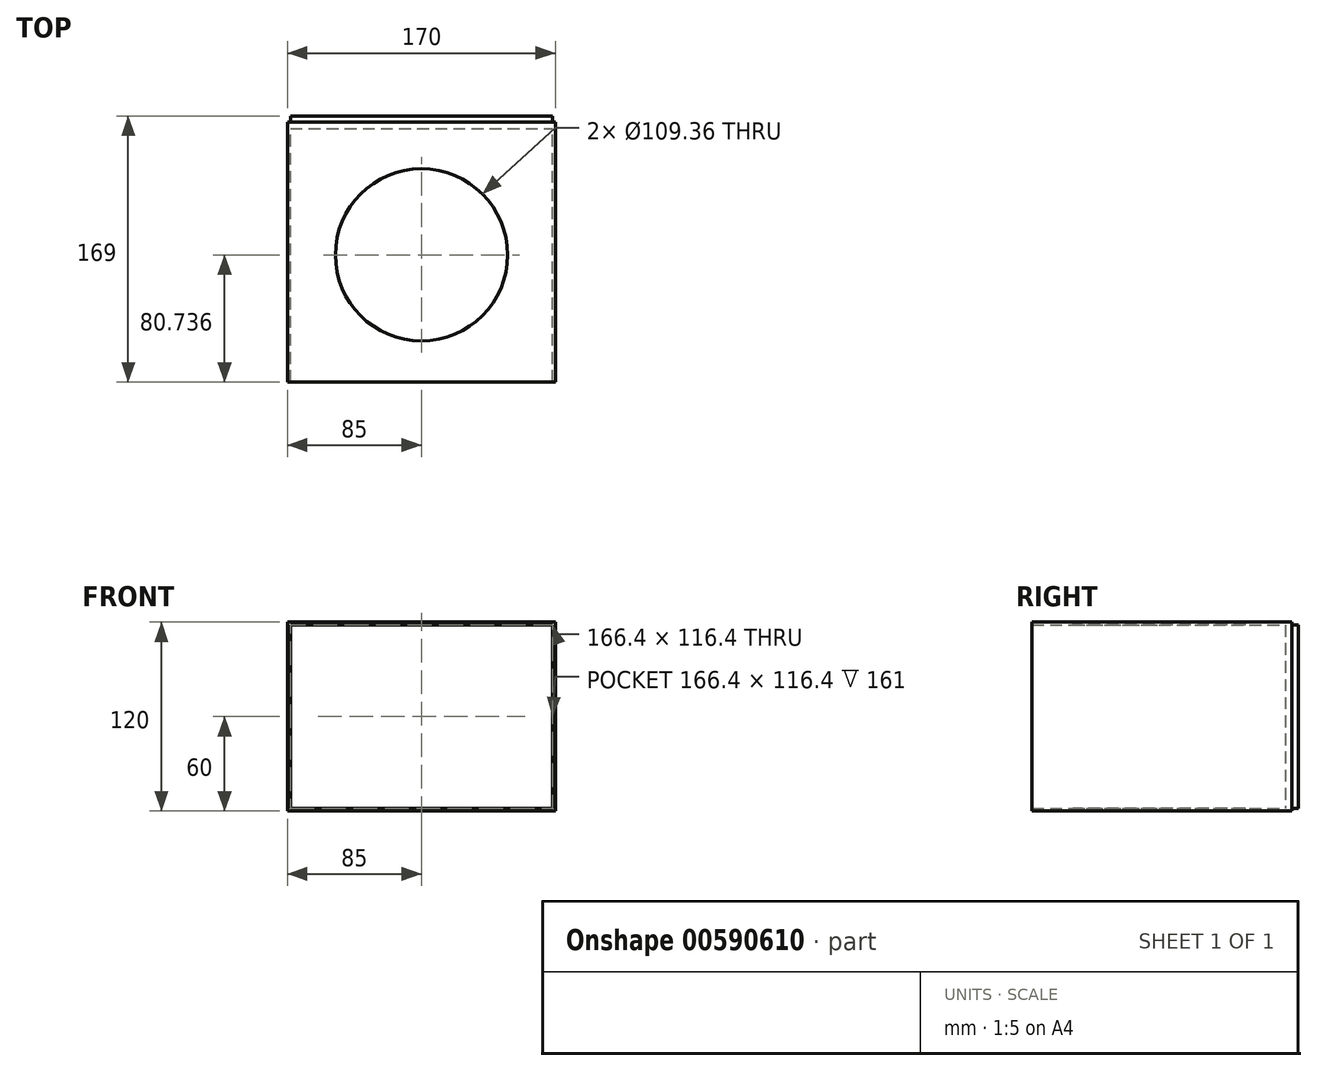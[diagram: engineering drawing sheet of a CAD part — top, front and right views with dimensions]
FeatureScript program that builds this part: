
annotation { "Feature Type Name" : "Feature", "Feature Type Description" : "" }
export const myFeature = defineFeature(function(context is Context, id is Id, definition is map)
    precondition{}
    {
        {
            var Q0;
            Q0=qCreatedBy(makeId("Front.planeOp"),FACE);
            var sketch = newSketch(context, id + "F0", { "sketchPlane" : qUnion([Q0])});
            skLineSegment(sketch, "E0.bottom", {"start": v(-85, 60) * mm, "end": v(85, 60) * mm});
            skLineSegment(sketch, "E0.top", {"start": v(-85, -60) * mm, "end": v(85, -60) * mm});
            skLineSegment(sketch, "E0.left", {"start": v(-85, 60) * mm, "end": v(-85, -60) * mm});
            skLineSegment(sketch, "E0.right", {"start": v(85, 60) * mm, "end": v(85, -60) * mm});
            skPoint(sketch, "E0.middle", {"position": v(0, 0) * mm});
            skLineSegment(sketch, "E1.0", {"start": v(-83.2, 58.2) * mm, "end": v(-83.2, -58.2) * mm});
            skLineSegment(sketch, "E1.1", {"start": v(-83.2, 58.2) * mm, "end": v(83.2, 58.2) * mm});
            skLineSegment(sketch, "E1.2", {"start": v(83.2, 58.2) * mm, "end": v(83.2, -58.2) * mm});
            skLineSegment(sketch, "E1.3", {"start": v(-83.2, -58.2) * mm, "end": v(83.2, -58.2) * mm});
            skSolve(sketch);
        }
        {
            var Q0;
            Q0=makeQuery(id+"F0.imprint","IMPRINT",FACE,{"disambiguationData":[TD([[makeQuery(id+"F0.imprint","IMPRINT",EDGE,{"derivedFrom":sQuery(id+"F0.wireOp",EDGE,"E0.bottom")}),-1.0]])]});
            extrude(context, id + "F1", {"entities" : qUnion([Q0]), "depth" : 165 * mm, "offsetDistance" : 25 * mm});
        }
        {
            var Q0;
            Q0=makeQuery(id+"F1.opExtrude","SWEPT_FACE",FACE,{"disambiguationData":[OSD([sQuery(id+"F0.wireOp",EDGE,"E0.bottom")])]});
            var sketch = newSketch(context, id + "F2", { "sketchPlane" : qUnion([Q0])});
            skSolve(sketch);
        }
        {
            var Q0;
            {var subQ0=sQuery(id+"F0.wireOp",EDGE,"E0.bottom");Q0=makeQuery(id+"F2.imprint","IMPRINT",FACE,{"disambiguationData":[TD([[makeQuery(id+"F2.imprint","IMPRINT",EDGE,{"derivedFrom":makeQuery(id+"F1.opExtrude","CAP_EDGE",EDGE,{"disambiguationData":[OSD([subQ0])],"isStart":true})}),-1.0]])]});}
            var sketch = newSketch(context, id + "F3", { "sketchPlane" : qUnion([Q0])});
            skCircle(sketch, "E2", {"center": v(0, -84.26) * mm, "radius": 54.68 * mm});
            skSolve(sketch);
        }
        {
            var Q0;
            Q0 = qSketchRegion(id + "F3", true);
            extrude(context, id + "F4", {"entities" : qUnion([Q0]), "endBound" : BoundingType.SYMMETRIC, "oppositeDirection" : true, "depth" : 318 * mm, "offsetDistance" : 25 * mm});
        }
        {
            var Q0;
            Q0=makeQuery(id+"F4.opExtrude","SWEPT_BODY",BODY,{"disambiguationData":[OSD([sQuery(id+"F3.wireOp",EDGE,"E2")])]});
            var Q1;
            Q1=makeQuery(id+"F1.opExtrude","SWEPT_BODY",BODY,{"disambiguationData":[OSD([sQuery(id+"F0.wireOp",EDGE,"E0.bottom"),sQuery(id+"F0.wireOp",EDGE,"E0.top"),sQuery(id+"F0.wireOp",EDGE,"E0.left"),sQuery(id+"F0.wireOp",EDGE,"E0.right"),sQuery(id+"F0.wireOp",EDGE,"E1.0"),sQuery(id+"F0.wireOp",EDGE,"E1.1"),sQuery(id+"F0.wireOp",EDGE,"E1.2"),sQuery(id+"F0.wireOp",EDGE,"E1.3")])]});
            booleanBodies(context, id + "F5", {"operationType" : BooleanOperationType.SUBTRACTION, "tools" : qUnion([Q0]), "targets" : qUnion([Q1])});
        }
        {
            var Q0;
            Q0=makeQuery(id+"F0.imprint","IMPRINT",FACE,{"disambiguationData":[TD([[makeQuery(id+"F0.imprint","IMPRINT",EDGE,{"derivedFrom":sQuery(id+"F0.wireOp",EDGE,"E1.0")}),1.0]])]});
            extrude(context, id + "F6", {"entities" : qUnion([Q0]), "operationType" : NewBodyOperationType.ADD, "endBound" : BoundingType.SYMMETRIC, "depth" : 8 * mm, "offsetDistance" : 25 * mm});
        }
    });
